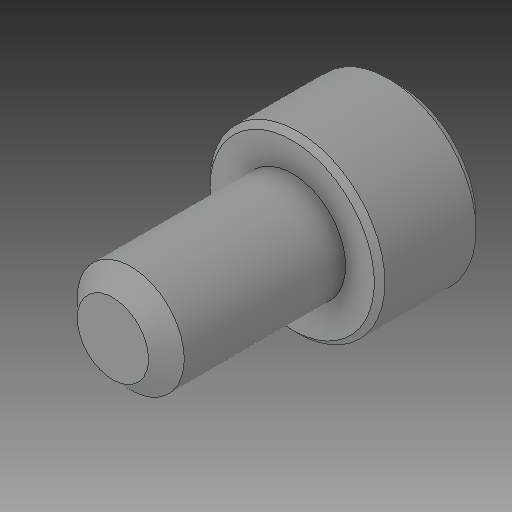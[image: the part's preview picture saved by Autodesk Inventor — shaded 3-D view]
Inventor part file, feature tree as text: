
AUTODESK INVENTOR PART (.ipt)
format: ipt  version: 2019 (Build 230136000, 136)  size: 134,144 bytes
history: native  units: in
note: dims shown in document units (in); Inventor stores cm internally (conversion verified against a paired STEP export)
features: chamfer x1
ambient origin geometry x8: Origin, YZ Plane, XZ Plane, XY Plane, X Axis, Y Axis, Z Axis, Center Point
bodies: Solid1 (feature_tree)
feature tree (1):
  chamfer  "Chamfer2"  [1 undecoded]
note: 1 required parameter value undecoded (feature->parameter linkage not recoverable at this tier; creation-order binding heuristic only, values carry confidence <= 0.55)
